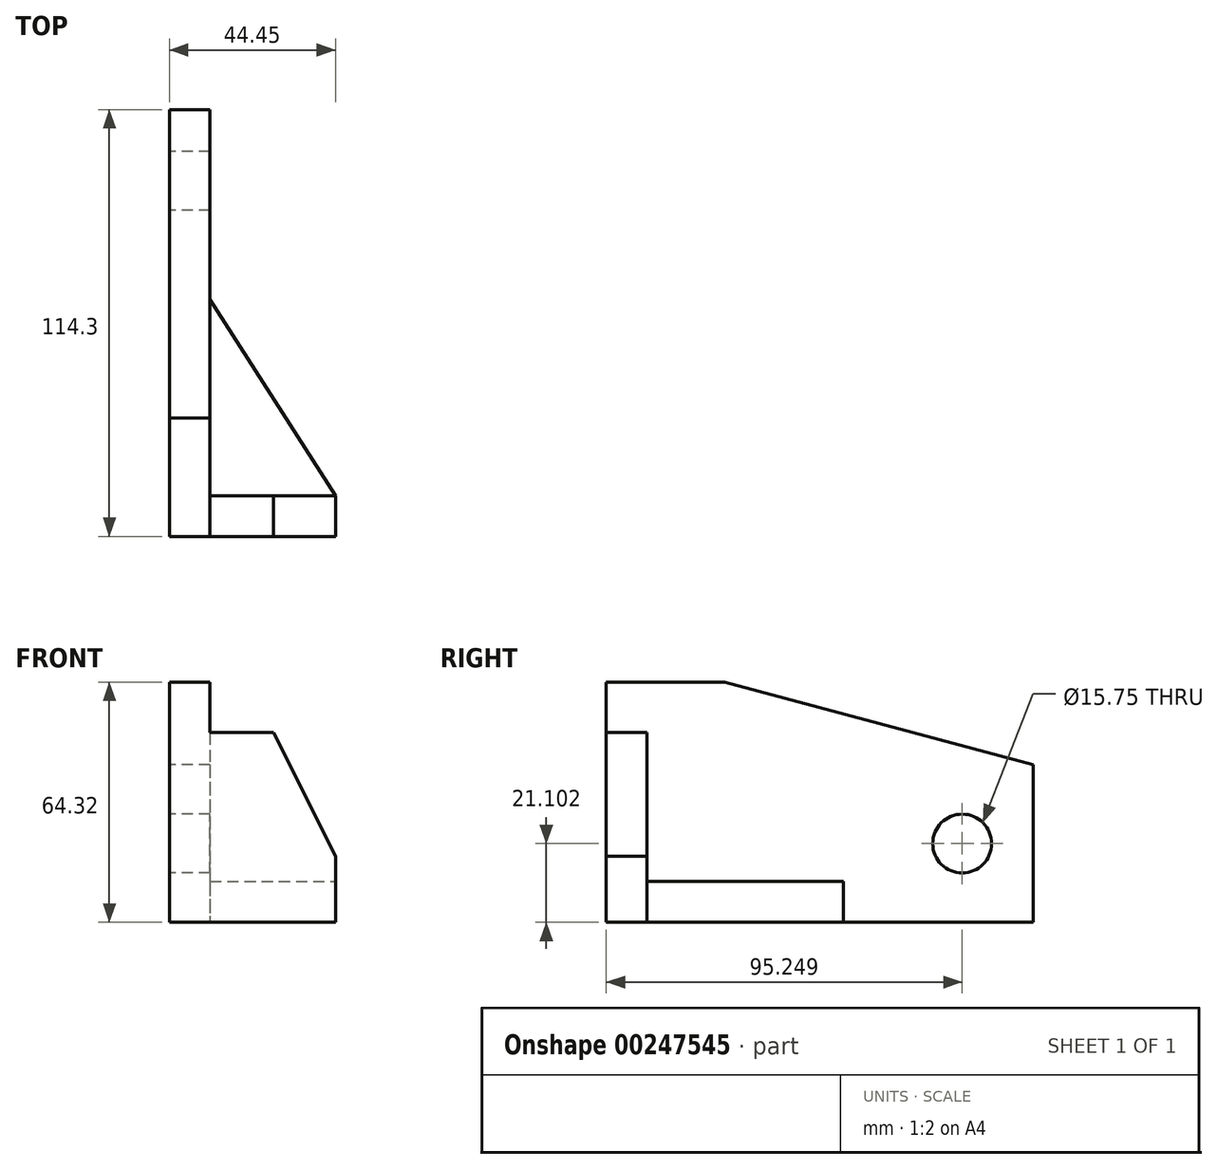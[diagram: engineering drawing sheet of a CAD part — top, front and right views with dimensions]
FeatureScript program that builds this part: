
annotation { "Feature Type Name" : "Feature", "Feature Type Description" : "" }
export const myFeature = defineFeature(function(context is Context, id is Id, definition is map)
    precondition{}
    {
        {
            var Q0;
            Q0=qCreatedBy(makeId("Right.planeOp"),FACE);
            var sketch = newSketch(context, id + "F0", { "sketchPlane" : qUnion([Q0])});
            skLineSegment(sketch, "E0", {"start": v(-73.15, 34.2) * mm, "end": v(-41.4, 34.2) * mm});
            skLineSegment(sketch, "E1", {"start": v(-41.4, 34.2) * mm, "end": v(41.15, 12.08) * mm});
            skLineSegment(sketch, "E2", {"start": v(-73.15, 20.68) * mm, "end": v(-62.23, 20.68) * mm});
            skLineSegment(sketch, "E3", {"start": v(-62.23, 20.68) * mm, "end": v(-62.23, -19.2) * mm});
            skLineSegment(sketch, "E4", {"start": v(-62.23, -19.2) * mm, "end": v(-9.65, -19.2) * mm});
            skLineSegment(sketch, "E5", {"start": v(-9.65, -19.2) * mm, "end": v(-9.65, -30.12) * mm});
            skLineSegment(sketch, "E6", {"start": v(-41.4, 34.2) * mm, "end": v(41.15, 34.2) * mm, "construction": true});
            skLineSegment(sketch, "E7", {"start": v(41.15, 34.2) * mm, "end": v(41.15, 12.08) * mm, "construction": true});
            skLineSegment(sketch, "E8", {"start": v(41.15, 12.08) * mm, "end": v(41.15, -30.12) * mm});
            skLineSegment(sketch, "E9", {"start": v(41.15, -9.02) * mm, "end": v(22.1, -9.02) * mm, "construction": true});
            skCircle(sketch, "E10", {"center": v(22.1, -9.02) * mm, "radius": 7.87 * mm});
            skLineSegment(sketch, "E11", {"start": v(-73.15, -30.12) * mm, "end": v(-9.65, -30.12) * mm});
            skLineSegment(sketch, "E12", {"start": v(-9.65, -30.12) * mm, "end": v(41.15, -30.12) * mm});
            skLineSegment(sketch, "E13", {"start": v(-62.23, -19.2) * mm, "end": v(-62.23, -30.12) * mm});
            skLineSegment(sketch, "E14", {"start": v(-73.15, 34.2) * mm, "end": v(-73.15, -30.12) * mm});
            skSolve(sketch);
        }
        {
            var Q0;
            Q0=makeQuery(id+"F0.imprint","IMPRINT",FACE,{"disambiguationData":[TD([[makeQuery(id+"F0.imprint","IMPRINT",EDGE,{"derivedFrom":sQuery(id+"F0.wireOp",EDGE,"E0")}),-1.0]])]});
            extrude(context, id + "F1", {"entities" : qUnion([Q0]), "depth" : 10.92 * mm});
        }
        {
            var Q0;
            Q0=makeQuery(id+"F0.imprint","IMPRINT",FACE,{"disambiguationData":[TD([[makeQuery(id+"F0.imprint","IMPRINT",EDGE,{"derivedFrom":sQuery(id+"F0.wireOp",EDGE,"E4")}),-1.0]])]});
            var Q1;
            {var subQ3=sQuery(id+"F0.wireOp",EDGE,"E13");Q1=makeQuery(id+"F0.imprint","IMPRINT",FACE,{"disambiguationData":[TD([[makeQuery(id+"F0.imprint","IMPRINT",EDGE,{"derivedFrom":subQ3}),-1.0]])]});}
            var Q2;
            {var subQ0=sQuery(id+"F0.wireOp",EDGE,"E2");Q2=makeQuery(id+"F0.imprint","IMPRINT",FACE,{"disambiguationData":[TD([[makeQuery(id+"F0.imprint","IMPRINT",EDGE,{"derivedFrom":subQ0}),-1.0]])]});}
            extrude(context, id + "F2", {"entities" : qUnion([Q0, Q1, Q2]), "operationType" : NewBodyOperationType.ADD, "depth" : 44.45 * mm});
        }
        {
            var Q0;
            Q0=makeQuery(id+"F2.opExtrude","CAP_EDGE",EDGE,{"disambiguationData":[OSD([sQuery(id+"F0.wireOp",EDGE,"E2")])],"isStart":false});
            chamfer(context, id + "F3", {"entities" : qUnion([Q0]), "chamferType" : ChamferType.TWO_OFFSETS, "width1" : 16.57 * mm, "oppositeDirection" : false, "width2" : 33.14 * mm, "tangentPropagation" : true});
        }
        {
            var Q0;
            Q0=makeQuery(id+"F2.opExtrude","CAP_EDGE",EDGE,{"disambiguationData":[OSD([sQuery(id+"F0.wireOp",EDGE,"E5")])],"isStart":false});
            chamfer(context, id + "F4", {"entities" : qUnion([Q0]), "chamferType" : ChamferType.OFFSET_ANGLE, "width" : 33.53 * mm, "oppositeDirection" : false, "angle" : 57.47 * degree, "tangentPropagation" : true});
        }
    });
